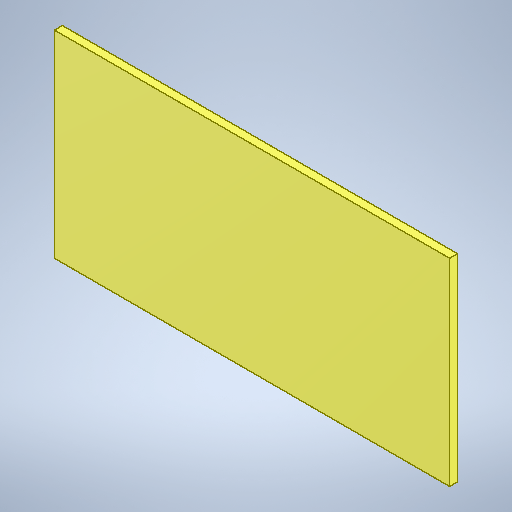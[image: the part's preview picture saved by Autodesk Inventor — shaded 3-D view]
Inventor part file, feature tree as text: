
AUTODESK INVENTOR PART (.ipt)
format: ipt  version: 2025.2 (Build 292293000, 293)  size: 204,288 bytes
history: native  units: mm
features: extrude x1, sketch x1
ambient origin geometry x8: Origin, YZ Plane, XZ Plane, XY Plane, X Axis, Y Axis, Z Axis, Center Point
bodies: Solid1 (feature_tree)
feature tree (2):
  extrude  "Extrusion1"  Depth=750.0mm
  sketch  "Sketch1"  dims[d0=1500.0mm d1=750.0mm d2=30.0mm d3=0.0mm]
